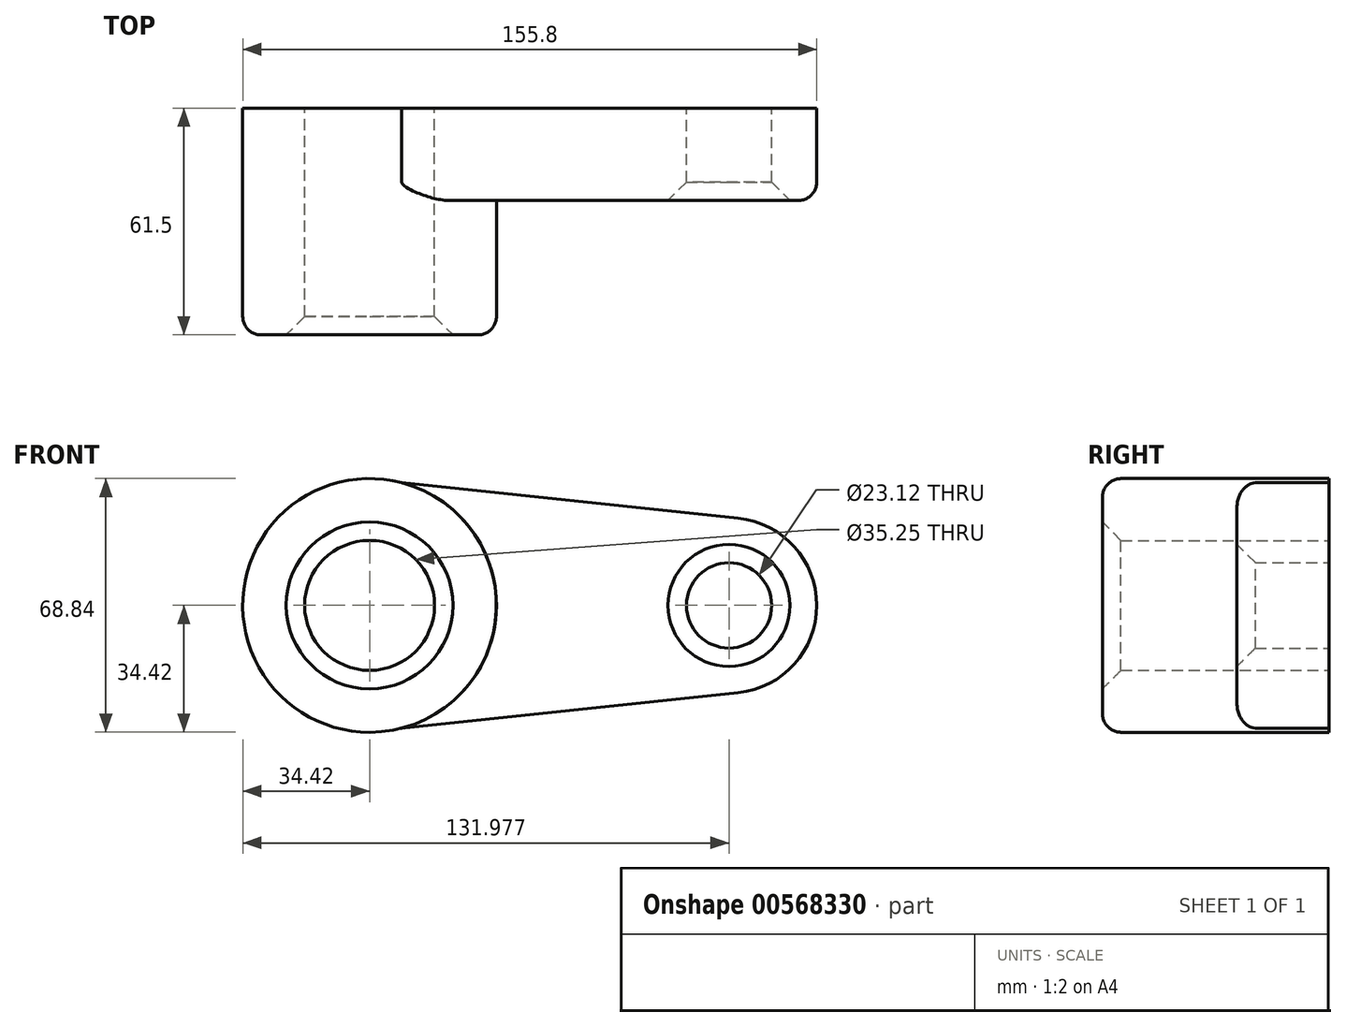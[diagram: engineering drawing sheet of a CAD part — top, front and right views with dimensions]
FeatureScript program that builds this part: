
annotation { "Feature Type Name" : "Feature", "Feature Type Description" : "" }
export const myFeature = defineFeature(function(context is Context, id is Id, definition is map)
    precondition{}
    {
        {
            var Q0;
            Q0=qCreatedBy(makeId("Front.planeOp"),FACE);
            var sketch = newSketch(context, id + "F0", { "sketchPlane" : qUnion([Q0])});
            skCircle(sketch, "E0", {"center": v(0, 0) * mm, "radius": 34.07 * mm});
            skCircle(sketch, "E1", {"center": v(97.56, 0) * mm, "radius": 23.82 * mm});
            skLineSegment(sketch, "E2", {"start": v(5.18, 33.67) * mm, "end": v(100.05, 23.69) * mm});
            skLineSegment(sketch, "E3", {"start": v(4.56, -33.76) * mm, "end": v(100.06, -23.69) * mm});
            skCircle(sketch, "E4", {"center": v(0, 0) * mm, "radius": 17.92 * mm});
            skCircle(sketch, "E5", {"center": v(97.56, 0) * mm, "radius": 11.56 * mm});
            skSolve(sketch);
        }
        {
            var Q0;
            Q0 = qSketchRegion(id + "F0", true);
            extrude(context, id + "F1", {"entities" : qUnion([Q0]), "depth" : 25 * mm, "offsetDistance" : 25 * mm});
        }
        {
            var Q0;
            Q0=qCreatedBy(makeId("Front.planeOp"),FACE);
            var sketch = newSketch(context, id + "F2", { "sketchPlane" : qUnion([Q0])});
            skCircle(sketch, "E6", {"center": v(0, 0) * mm, "radius": 34.42 * mm});
            skCircle(sketch, "E7", {"center": v(0, 0) * mm, "radius": 17.63 * mm});
            skSolve(sketch);
        }
        {
            var Q0;
            Q0=makeQuery(id+"F2.imprint","IMPRINT",FACE,{"disambiguationData":[TD([[makeQuery(id+"F2.imprint","IMPRINT",EDGE,{"derivedFrom":sQuery(id+"F2.wireOp",EDGE,"E6")}),1.0]])]});
            extrude(context, id + "F3", {"entities" : qUnion([Q0]), "operationType" : NewBodyOperationType.ADD, "depth" : 61.5 * mm, "offsetDistance" : 25 * mm});
        }
        {
            var Q0;
            Q0=makeQuery(id+"F3.opExtrude","CAP_EDGE",EDGE,{"disambiguationData":[OSD([sQuery(id+"F2.wireOp",EDGE,"E6")])],"isStart":false});
            fillet(context, id + "F4", {"entities" : qUnion([Q0]), "radius" : 5 * mm, "tangentPropagation" : true, "allowEdgeOverflow" : false});
        }
        {
            var Q0;
            Q0=makeQuery(id+"F3.opExtrude","CAP_EDGE",EDGE,{"disambiguationData":[OSD([sQuery(id+"F2.wireOp",EDGE,"E7")])],"isStart":false});
            chamfer(context, id + "F5", {"entities" : qUnion([Q0]), "width" : 5 * mm, "tangentPropagation" : true});
        }
        {
            var Q0;
            Q0=makeQuery(id+"F1.opExtrude","CAP_EDGE",EDGE,{"disambiguationData":[OSD([sQuery(id+"F0.wireOp",EDGE,"E5")])],"isStart":false});
            chamfer(context, id + "F6", {"entities" : qUnion([Q0]), "width" : 5 * mm, "tangentPropagation" : true});
        }
        {
            var Q0;
            Q0=makeQuery(id+"F1.opExtrude","CAP_EDGE",EDGE,{"disambiguationData":[OSD([sQuery(id+"F0.wireOp",EDGE,"E3")])],"isStart":false});
            fillet(context, id + "F7", {"entities" : qUnion([Q0]), "radius" : 5 * mm, "tangentPropagation" : true, "allowEdgeOverflow" : false});
        }
    });
